# Revit family: 19 Zoll Switch MS400995M
name_source: partatom
category: Datengeräte
units: mm (PartAtom-declared; Revit-internal decimal feet)

## family parameters
Arbeitsebenenbasiert = Nein
Beim Laden mit Abzugskörper schneiden = Nein
Bemaßung runder Anschluss = Durchmesser verwenden
Beschriftungsausrichtung beibehalten = Nein
Gemeinsam genutzt = Nein
Immer vertikal = Ja
OmniClass-Nummer = 23.85.50.17
OmniClass-Titel = Communication and Data Processing Equipment
Raumberechnungspunkt = Nein
Teiletyp = Normal

## types (1)
- 19 Zoll Switch MS400995M
    Anschluss 1 = 2x 40G QSFP+ Slots
    Anschluss 2 = 20x 1/10G SFP+ Slots
    Anschluss 3 = 4x 10G/25GBase-X SFP28-Slots
    Anschluss 4 = Konsolenport (RJ-45)
    Artikelnummer = MS400995M
    Ausführung = managed switch L3
    Beschreibung = 26-Port 40G Multi 1/10G Fiber L3 Switch 19"
    Hersteller = MICROSENS
    Material = Edelstahl AISI 304
    Material 2 = Stahl, lackierte Oberfläche, dunkelgrau, matt
    Spannung Input = 100~240VAC (C14)
    Vorgabe-Ansicht = 0 mm
